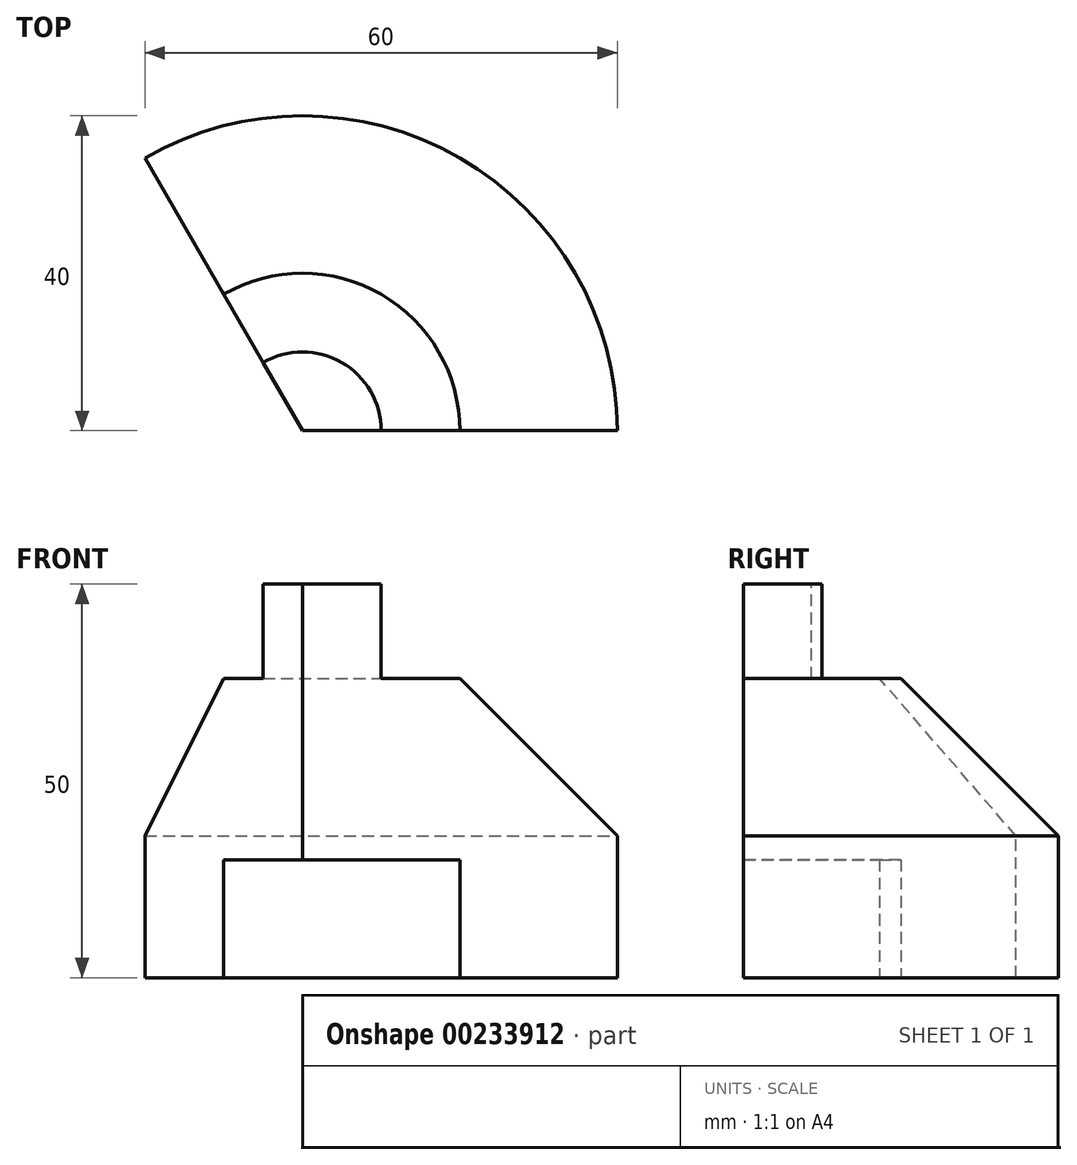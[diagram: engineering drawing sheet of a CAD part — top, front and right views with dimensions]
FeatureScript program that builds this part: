
annotation { "Feature Type Name" : "Feature", "Feature Type Description" : "" }
export const myFeature = defineFeature(function(context is Context, id is Id, definition is map)
    precondition{}
    {
        {
            var Q0;
            Q0=qCreatedBy(makeId("Front.planeOp"),FACE);
            var sketch = newSketch(context, id + "F0", { "sketchPlane" : qUnion([Q0])});
            skLineSegment(sketch, "E0", {"start": v(-111.43, 0) * mm, "end": v(110.29, 0) * mm});
            skLineSegment(sketch, "E1", {"start": v(0, 0) * mm, "end": v(0, 112) * mm});
            skLineSegment(sketch, "E2", {"start": v(20, 15) * mm, "end": v(20, 0) * mm});
            skLineSegment(sketch, "E3", {"start": v(40, 0) * mm, "end": v(40, 18) * mm});
            skLineSegment(sketch, "E4", {"start": v(40, 18) * mm, "end": v(20, 38) * mm});
            skLineSegment(sketch, "E5", {"start": v(20, 38) * mm, "end": v(10, 38) * mm});
            skLineSegment(sketch, "E6", {"start": v(10, 38) * mm, "end": v(10, 50) * mm});
            skLineSegment(sketch, "E7", {"start": v(10, 50) * mm, "end": v(0, 50) * mm});
            skLineSegment(sketch, "E8", {"start": v(0, 15) * mm, "end": v(20, 15) * mm});
            skSolve(sketch);
        }
        {
            var Q0;
            {var subQ1=sQuery(id+"F0.wireOp",EDGE,"E2");Q0=makeQuery(id+"F0.imprint","IMPRINT",FACE,{"disambiguationData":[TD([[makeQuery(id+"F0.imprint","IMPRINT",EDGE,{"derivedFrom":subQ1}),1.0]])]});}
            var Q1;
            Q1=sQuery(id+"F0.wireOp",EDGE,"E1");
            revolve(context, id + "F1", {"entities" : qUnion([Q0]), "axis" : qUnion([Q1]), "revolveType" : RevolveType.ONE_DIRECTION, "angle" : 120 * degree});
        }
    });
